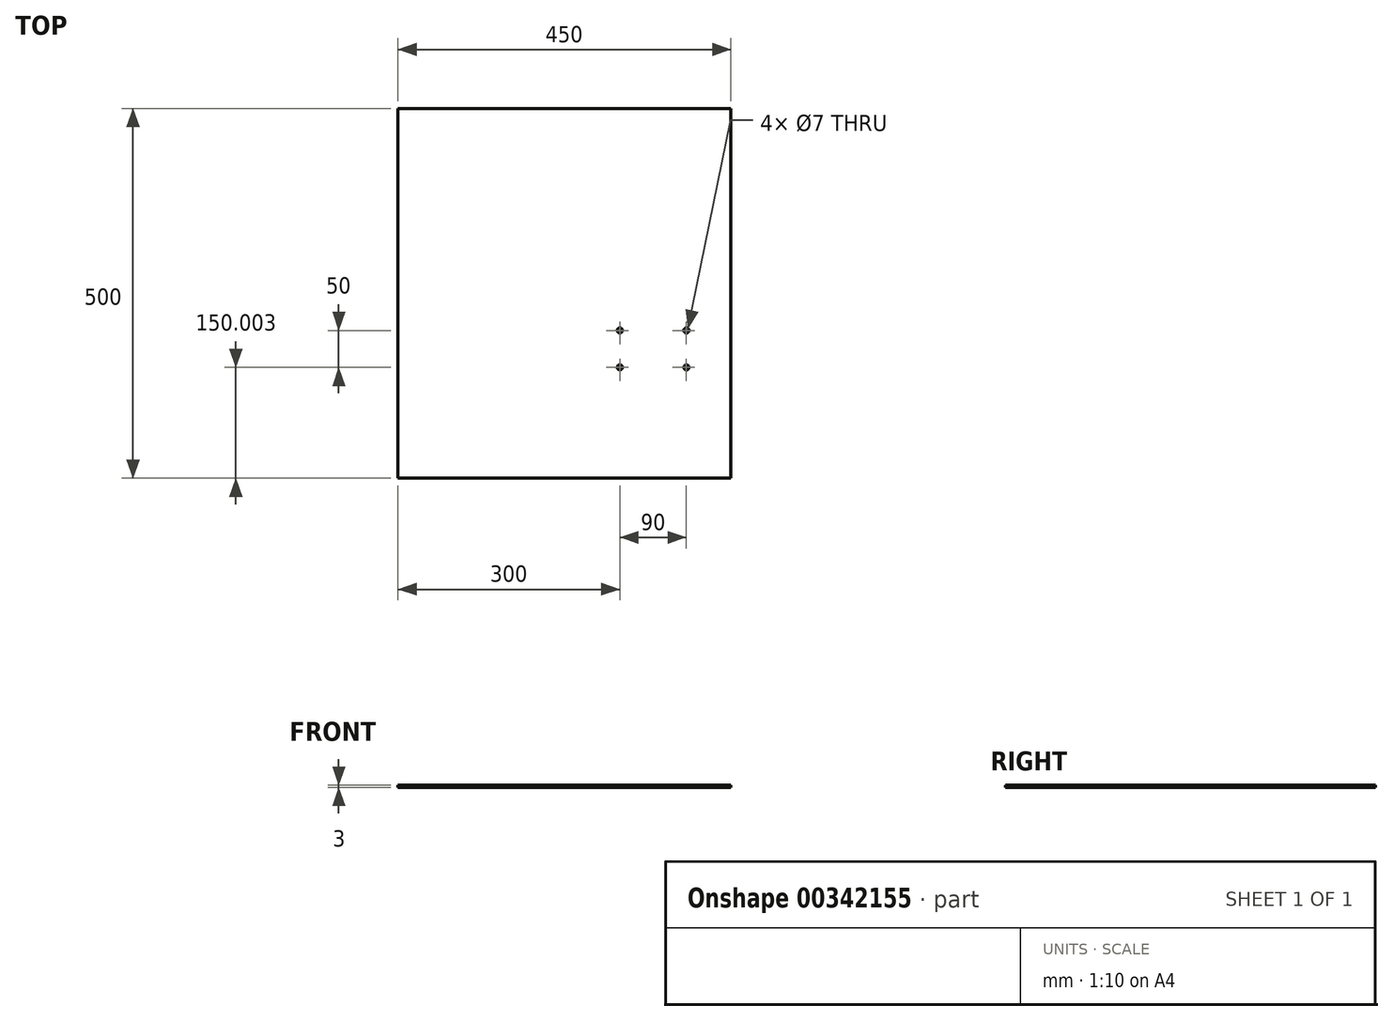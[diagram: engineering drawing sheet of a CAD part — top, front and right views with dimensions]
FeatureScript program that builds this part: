
annotation { "Feature Type Name" : "Feature", "Feature Type Description" : "" }
export const myFeature = defineFeature(function(context is Context, id is Id, definition is map)
    precondition{}
    {
        {
            var Q0;
            Q0=qCreatedBy(makeId("Top.planeOp"),FACE);
            var sketch = newSketch(context, id + "F0", { "sketchPlane" : qUnion([Q0])});
            skLineSegment(sketch, "E0.bottom", {"start": v(225, 199.78) * mm, "end": v(-225, 199.78) * mm});
            skLineSegment(sketch, "E0.top", {"start": v(225, -300.22) * mm, "end": v(-225, -300.22) * mm});
            skLineSegment(sketch, "E0.left", {"start": v(225, 199.78) * mm, "end": v(225, -300.22) * mm});
            skLineSegment(sketch, "E0.right", {"start": v(-225, 199.78) * mm, "end": v(-225, -300.22) * mm});
            skCircle(sketch, "E1", {"center": v(75, -150.22) * mm, "radius": 3.5 * mm});
            skCircle(sketch, "E2", {"center": v(165, -100.22) * mm, "radius": 3.5 * mm});
            skCircle(sketch, "E3", {"center": v(75, -100.22) * mm, "radius": 3.5 * mm});
            skLineSegment(sketch, "E4.bottom", {"start": v(75, -150.22) * mm, "end": v(165, -150.22) * mm});
            skLineSegment(sketch, "E4.top", {"start": v(75, -100.22) * mm, "end": v(165, -100.22) * mm});
            skLineSegment(sketch, "E4.left", {"start": v(75, -100.22) * mm, "end": v(75, -150.22) * mm});
            skLineSegment(sketch, "E4.right", {"start": v(165, -100.22) * mm, "end": v(165, -150.22) * mm});
            skCircle(sketch, "E5", {"center": v(165, -150.22) * mm, "radius": 3.5 * mm});
            skSolve(sketch);
        }
        {
            var Q0;
            Q0=qSketchRegion(id+"F0",true);
            var Q1;
            {var subQ5=sQuery(id+"F0.wireOp",EDGE,"E4.bottom");var subQ6=sQuery(id+"F0.wireOp",EDGE,"E1");var subQ7=makeQuery(id+"F0.imprint","INTERSECT",VERTEX,{"derivedFrom":[subQ6,subQ5]});Q1=makeQuery(id+"F0.imprint","IMPRINT",FACE,{"disambiguationData":[TD([[makeQuery(id+"F0.imprint","IMPRINT",EDGE,{"disambiguationData":[TD([[subQ7,1.0]])],"derivedFrom":subQ6}),-1.0]])]});}
            var Q2;
            {var subQ0=sQuery(id+"F0.wireOp",EDGE,"E4.bottom");var subQ1=sQuery(id+"F0.wireOp",EDGE,"E1");var subQ2=makeQuery(id+"F0.imprint","INTERSECT",VERTEX,{"derivedFrom":[subQ1,subQ0]});Q2=makeQuery(id+"F0.imprint","IMPRINT",FACE,{"disambiguationData":[TD([[makeQuery(id+"F0.imprint","IMPRINT",EDGE,{"disambiguationData":[TD([[subQ2,-1.0]])],"derivedFrom":subQ1}),-1.0]])]});}
            extrude(context, id + "F1", {"entities" : qUnion([Q0, Q1, Q2]), "depth" : 3 * mm});
        }
    });
